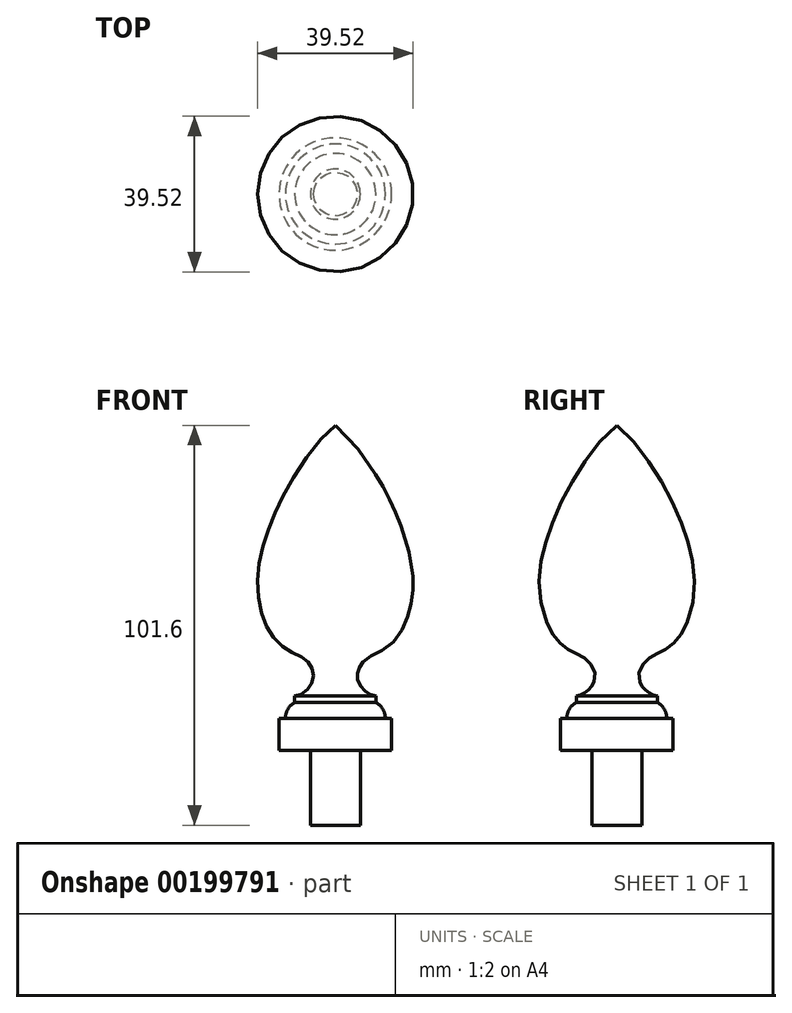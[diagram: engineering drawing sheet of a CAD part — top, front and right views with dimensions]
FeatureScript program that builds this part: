
annotation { "Feature Type Name" : "Feature", "Feature Type Description" : "" }
export const myFeature = defineFeature(function(context is Context, id is Id, definition is map)
    precondition{}
    {
        {
            var Q0;
            Q0=qCreatedBy(makeId("Front.planeOp"),FACE);
            var sketch = newSketch(context, id + "F0", { "sketchPlane" : qUnion([Q0])});
            skLineSegment(sketch, "E0", {"start": v(0, 0) * mm, "end": v(-14.29, 0) * mm});
            skLineSegment(sketch, "E1", {"start": v(-14.29, 0) * mm, "end": v(-14.29, 8.06) * mm});
            skPoint(sketch, "E2", {"position": v(0, 82.55) * mm});
            skLineSegment(sketch, "E3", {"start": v(-14.29, 8.06) * mm, "end": v(-12.7, 8.06) * mm});
            skArc(sketch, "E4", {"start": v(-10.32, 12.19) * mm, "mid": v(-12.06, 10.45) * mm, "end": v(-12.7, 8.06) * mm});
            skLineSegment(sketch, "E5", {"start": v(-10.32, 12.19) * mm, "end": v(-10.32, 13.78) * mm});
            skPoint(sketch, "E6.14.internal.snap0", {"position": v(-7.14, 0) * mm});
            skFitSpline(sketch, "E6", {"points": [v(-10.32, 13.78) * mm, v(-8.8, 14.21) * mm, v(-6.88, 15.68) * mm, v(-5.88, 17.32) * mm, v(-5.58, 19.5) * mm, v(-6.41, 21.57) * mm, v(-7.95, 23.27) * mm, v(-11.23, 25) * mm, v(-15.45, 28.29) * mm, v(-18.6, 34.58) * mm, v(-19.7, 44.47) * mm, v(-17.07, 55.81) * mm, v(-11.6, 67.76) * mm, v(0, 82.55) * mm], "startDerivative": vector(40.6, 10.22) * mm, "endDerivative": vector(80.76, 59.17) * mm});
            skLineSegment(sketch, "E7", {"start": v(0, 82.55) * mm, "end": v(0, 0) * mm});
            skSolve(sketch);
        }
        {
            var Q0;
            Q0=makeQuery(id+"F0.imprint","IMPRINT",FACE,{"disambiguationData":[TD([[makeQuery(id+"F0.imprint","IMPRINT",EDGE,{"derivedFrom":sQuery(id+"F0.wireOp",EDGE,"E0")}),-1.0]])]});
            var Q1;
            Q1=sQuery(id+"F0.wireOp",EDGE,"E7");
            revolve(context, id + "F1", {"entities" : qUnion([Q0]), "axis" : qUnion([Q1]), "revolveType" : RevolveType.FULL});
        }
        {
            var Q0;
            Q0=makeQuery(id+"F1.opRevolve","SWEPT_FACE",FACE,{"disambiguationData":[OSD([sQuery(id+"F0.wireOp",EDGE,"E0")])]});
            var sketch = newSketch(context, id + "F2", { "sketchPlane" : qUnion([Q0])});
            skCircle(sketch, "E8", {"center": v(0, 0) * mm, "radius": 6.35 * mm});
            skSolve(sketch);
        }
        {
            var Q0;
            Q0 = qSketchRegion(id + "F2", true);
            extrude(context, id + "F3", {"entities" : qUnion([Q0]), "operationType" : NewBodyOperationType.ADD, "depth" : 19.05 * mm});
        }
        {
            var Q0;
            Q0=qCreatedBy(makeId("Top.planeOp"),FACE);
            cPlane(context, id + "F4", {"entities" : qUnion([Q0]), "cplaneType" : CPlaneType.OFFSET, "offset" : 101.6 * mm, "width" : 152.4 * mm, "height" : 152.4 * mm});
        }
        {
            var Q0;
            Q0=qCreatedBy(makeId("Top.planeOp"),FACE);
            var sketch = newSketch(context, id + "F5", { "sketchPlane" : qUnion([Q0])});
            skCircle(sketch, "E9.cCircle", {"center": v(0, 0) * mm, "radius": 38.28 * mm, "construction": true});
            skLineSegment(sketch, "E9.0", {"start": v(21.27, -31.83) * mm, "end": v(14.65, -35.37) * mm});
            skLineSegment(sketch, "E9.1", {"start": v(14.65, -35.37) * mm, "end": v(7.47, -37.55) * mm});
            skLineSegment(sketch, "E9.2", {"start": v(7.47, -37.55) * mm, "end": v(0, -38.28) * mm});
            skLineSegment(sketch, "E9.3", {"start": v(0, -38.28) * mm, "end": v(-7.47, -37.55) * mm});
            skLineSegment(sketch, "E9.4", {"start": v(-7.47, -37.55) * mm, "end": v(-14.65, -35.37) * mm});
            skLineSegment(sketch, "E9.5", {"start": v(-14.65, -35.37) * mm, "end": v(-21.27, -31.83) * mm});
            skLineSegment(sketch, "E9.6", {"start": v(-21.27, -31.83) * mm, "end": v(-27.07, -27.07) * mm});
            skLineSegment(sketch, "E9.7", {"start": v(-27.07, -27.07) * mm, "end": v(-31.83, -21.27) * mm});
            skLineSegment(sketch, "E9.8", {"start": v(-31.83, -21.27) * mm, "end": v(-35.37, -14.65) * mm});
            skLineSegment(sketch, "E9.9", {"start": v(-35.37, -14.65) * mm, "end": v(-37.55, -7.47) * mm});
            skLineSegment(sketch, "E9.10", {"start": v(-37.55, -7.47) * mm, "end": v(-38.28, 0) * mm});
            skLineSegment(sketch, "E9.11", {"start": v(-38.28, 0) * mm, "end": v(-37.55, 7.47) * mm});
            skLineSegment(sketch, "E9.12", {"start": v(-37.55, 7.47) * mm, "end": v(-35.37, 14.65) * mm});
            skLineSegment(sketch, "E9.13", {"start": v(-35.37, 14.65) * mm, "end": v(-31.83, 21.27) * mm});
            skLineSegment(sketch, "E9.14", {"start": v(-31.83, 21.27) * mm, "end": v(-27.07, 27.07) * mm});
            skLineSegment(sketch, "E9.15", {"start": v(-27.07, 27.07) * mm, "end": v(-21.27, 31.83) * mm});
            skLineSegment(sketch, "E9.16", {"start": v(-21.27, 31.83) * mm, "end": v(-14.65, 35.37) * mm});
            skLineSegment(sketch, "E9.17", {"start": v(-14.65, 35.37) * mm, "end": v(-7.47, 37.55) * mm});
            skLineSegment(sketch, "E9.18", {"start": v(-7.47, 37.55) * mm, "end": v(0, 38.28) * mm});
            skLineSegment(sketch, "E9.19", {"start": v(0, 38.28) * mm, "end": v(7.47, 37.55) * mm});
            skLineSegment(sketch, "E9.20", {"start": v(7.47, 37.55) * mm, "end": v(14.65, 35.37) * mm});
            skLineSegment(sketch, "E9.21", {"start": v(14.65, 35.37) * mm, "end": v(21.27, 31.83) * mm});
            skLineSegment(sketch, "E9.22", {"start": v(21.27, 31.83) * mm, "end": v(27.07, 27.07) * mm});
            skLineSegment(sketch, "E9.23", {"start": v(27.07, 27.07) * mm, "end": v(31.83, 21.27) * mm});
            skLineSegment(sketch, "E9.24", {"start": v(31.83, 21.27) * mm, "end": v(35.37, 14.65) * mm});
            skLineSegment(sketch, "E9.25", {"start": v(35.37, 14.65) * mm, "end": v(37.55, 7.47) * mm});
            skLineSegment(sketch, "E9.26", {"start": v(37.55, 7.47) * mm, "end": v(38.28, 0) * mm});
            skLineSegment(sketch, "E9.27", {"start": v(38.28, 0) * mm, "end": v(37.55, -7.47) * mm});
            skLineSegment(sketch, "E9.28", {"start": v(37.55, -7.47) * mm, "end": v(35.37, -14.65) * mm});
            skLineSegment(sketch, "E9.29", {"start": v(35.37, -14.65) * mm, "end": v(31.83, -21.27) * mm});
            skLineSegment(sketch, "E9.30", {"start": v(31.83, -21.27) * mm, "end": v(27.07, -27.07) * mm});
            skLineSegment(sketch, "E9.31", {"start": v(27.07, -27.07) * mm, "end": v(21.27, -31.83) * mm});
            skLineSegment(sketch, "E10", {"start": v(0, 0) * mm, "end": v(44, 0) * mm, "construction": true});
            skSolve(sketch);
        }
        {
            var Q0;
            Q0=qCreatedBy(id+"F4.planeOp",FACE);
            var sketch = newSketch(context, id + "F6", { "sketchPlane" : qUnion([Q0])});
            skCircle(sketch, "E11.cCircle", {"center": v(0, 0) * mm, "radius": 38.28 * mm, "construction": true});
            skLineSegment(sketch, "E11.0", {"start": v(-7.47, -37.55) * mm, "end": v(-14.65, -35.37) * mm});
            skLineSegment(sketch, "E11.1", {"start": v(-14.65, -35.37) * mm, "end": v(-21.27, -31.83) * mm});
            skLineSegment(sketch, "E11.2", {"start": v(-21.27, -31.83) * mm, "end": v(-27.07, -27.07) * mm});
            skLineSegment(sketch, "E11.3", {"start": v(-27.07, -27.07) * mm, "end": v(-31.83, -21.27) * mm});
            skLineSegment(sketch, "E11.4", {"start": v(-31.83, -21.27) * mm, "end": v(-35.37, -14.65) * mm});
            skLineSegment(sketch, "E11.5", {"start": v(-35.37, -14.65) * mm, "end": v(-37.55, -7.47) * mm});
            skLineSegment(sketch, "E11.6", {"start": v(-37.55, -7.47) * mm, "end": v(-38.28, 0) * mm});
            skLineSegment(sketch, "E11.7", {"start": v(-38.28, 0) * mm, "end": v(-37.55, 7.47) * mm});
            skLineSegment(sketch, "E11.8", {"start": v(-37.55, 7.47) * mm, "end": v(-35.37, 14.65) * mm});
            skLineSegment(sketch, "E11.9", {"start": v(-35.37, 14.65) * mm, "end": v(-31.83, 21.27) * mm});
            skLineSegment(sketch, "E11.10", {"start": v(-31.83, 21.27) * mm, "end": v(-27.07, 27.07) * mm});
            skLineSegment(sketch, "E11.11", {"start": v(-27.07, 27.07) * mm, "end": v(-21.27, 31.83) * mm});
            skLineSegment(sketch, "E11.12", {"start": v(-21.27, 31.83) * mm, "end": v(-14.65, 35.37) * mm});
            skLineSegment(sketch, "E11.13", {"start": v(-14.65, 35.37) * mm, "end": v(-7.47, 37.55) * mm});
            skLineSegment(sketch, "E11.14", {"start": v(-7.47, 37.55) * mm, "end": v(0, 38.28) * mm});
            skLineSegment(sketch, "E11.15", {"start": v(0, 38.28) * mm, "end": v(7.47, 37.55) * mm});
            skLineSegment(sketch, "E11.16", {"start": v(7.47, 37.55) * mm, "end": v(14.65, 35.37) * mm});
            skLineSegment(sketch, "E11.17", {"start": v(14.65, 35.37) * mm, "end": v(21.27, 31.83) * mm});
            skLineSegment(sketch, "E11.18", {"start": v(21.27, 31.83) * mm, "end": v(27.07, 27.07) * mm});
            skLineSegment(sketch, "E11.19", {"start": v(27.07, 27.07) * mm, "end": v(31.83, 21.27) * mm});
            skLineSegment(sketch, "E11.20", {"start": v(31.83, 21.27) * mm, "end": v(35.37, 14.65) * mm});
            skLineSegment(sketch, "E11.21", {"start": v(35.37, 14.65) * mm, "end": v(37.55, 7.47) * mm});
            skLineSegment(sketch, "E11.22", {"start": v(37.55, 7.47) * mm, "end": v(38.28, 0) * mm});
            skLineSegment(sketch, "E11.23", {"start": v(38.28, 0) * mm, "end": v(37.55, -7.47) * mm});
            skLineSegment(sketch, "E11.24", {"start": v(37.55, -7.47) * mm, "end": v(35.37, -14.65) * mm});
            skLineSegment(sketch, "E11.25", {"start": v(35.37, -14.65) * mm, "end": v(31.83, -21.27) * mm});
            skLineSegment(sketch, "E11.26", {"start": v(31.83, -21.27) * mm, "end": v(27.07, -27.07) * mm});
            skLineSegment(sketch, "E11.27", {"start": v(27.07, -27.07) * mm, "end": v(21.27, -31.83) * mm});
            skLineSegment(sketch, "E11.28", {"start": v(21.27, -31.83) * mm, "end": v(14.65, -35.37) * mm});
            skLineSegment(sketch, "E11.29", {"start": v(14.65, -35.37) * mm, "end": v(7.47, -37.55) * mm});
            skLineSegment(sketch, "E11.30", {"start": v(7.47, -37.55) * mm, "end": v(0, -38.28) * mm});
            skLineSegment(sketch, "E11.31", {"start": v(0, -38.28) * mm, "end": v(-7.47, -37.55) * mm});
            skLineSegment(sketch, "E12", {"start": v(0, 0) * mm, "end": v(43.72, 0) * mm, "construction": true});
            skLineSegment(sketch, "E13", {"start": v(38.28, 0) * mm, "end": v(38.28, 0) * mm});
            skSolve(sketch);
        }
        {
            var Q0;
            Q0=qCreatedBy(makeId("Front.planeOp"),FACE);
            var sketch = newSketch(context, id + "F7", { "sketchPlane" : qUnion([Q0])});
            skLineSegment(sketch, "E14", {"start": v(38.28, 101.6) * mm, "end": v(38.28, 0) * mm, "construction": true});
            skSolve(sketch);
        }
    });
